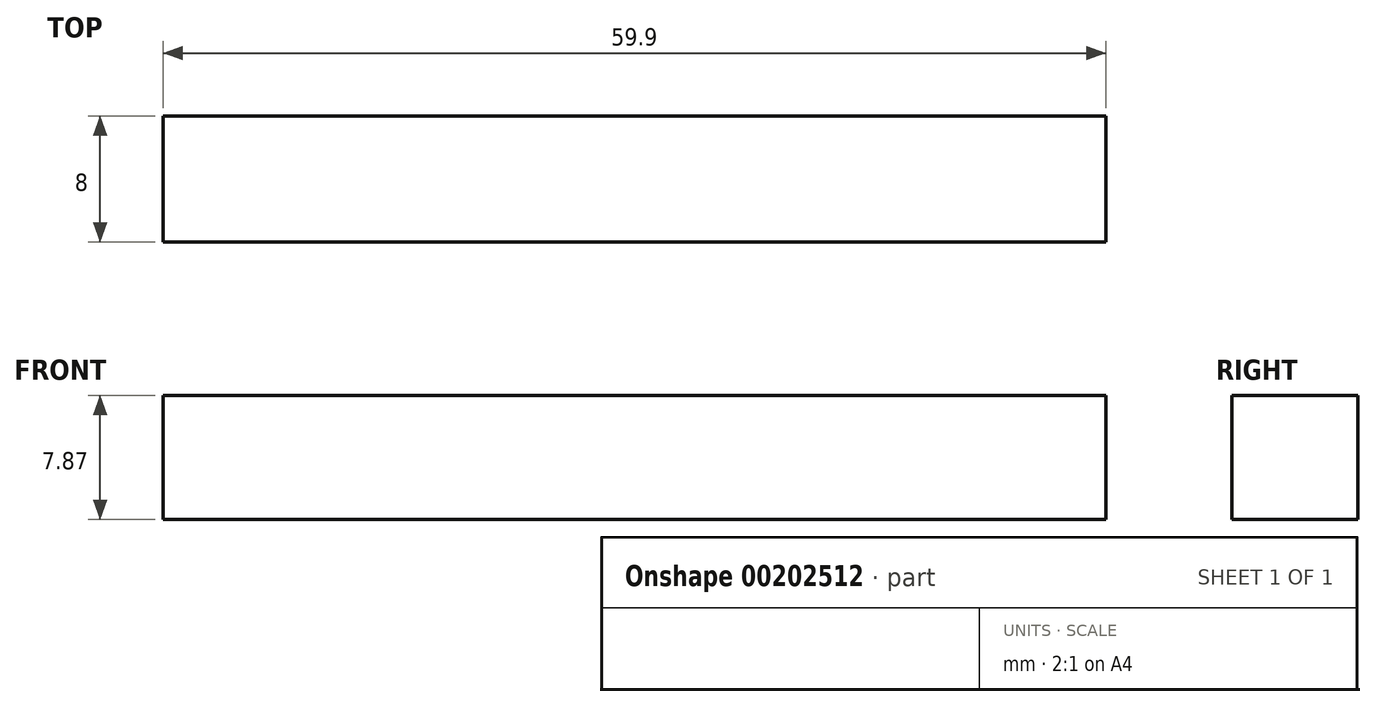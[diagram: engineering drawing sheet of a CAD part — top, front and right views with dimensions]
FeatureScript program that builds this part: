
annotation { "Feature Type Name" : "Feature", "Feature Type Description" : "" }
export const myFeature = defineFeature(function(context is Context, id is Id, definition is map)
    precondition{}
    {
        {
            var Q0;
            Q0=qCreatedBy(makeId("Top.planeOp"),FACE);
            var sketch = newSketch(context, id + "F0", { "sketchPlane" : qUnion([Q0])});
            skLineSegment(sketch, "E0.bottom", {"start": v(45.1, 47.95) * mm, "end": v(-45.1, 47.95) * mm});
            skLineSegment(sketch, "E0.top", {"start": v(45.1, -47.95) * mm, "end": v(-45.1, -47.95) * mm});
            skLineSegment(sketch, "E0.left", {"start": v(45.1, 47.95) * mm, "end": v(45.1, -47.95) * mm});
            skLineSegment(sketch, "E0.right", {"start": v(-45.1, 47.95) * mm, "end": v(-45.1, -47.95) * mm});
            skPoint(sketch, "E0.middle", {"position": v(0, 0) * mm});
            skLineSegment(sketch, "E1.bottom", {"start": v(29.95, 39.05) * mm, "end": v(-29.95, 39.05) * mm});
            skLineSegment(sketch, "E1.top", {"start": v(29.95, 47.05) * mm, "end": v(-29.95, 47.05) * mm});
            skLineSegment(sketch, "E1.left", {"start": v(29.95, 39.05) * mm, "end": v(29.95, 47.05) * mm});
            skLineSegment(sketch, "E1.right", {"start": v(-29.95, 39.05) * mm, "end": v(-29.95, 47.05) * mm});
            skPoint(sketch, "E1.middle", {"position": v(0, 43.05) * mm});
            skSolve(sketch);
        }
        {
            var Q0;
            Q0=makeQuery(id+"F0.imprint","IMPRINT",FACE,{"disambiguationData":[TD([[makeQuery(id+"F0.imprint","IMPRINT",EDGE,{"derivedFrom":sQuery(id+"F0.wireOp",EDGE,"E1.bottom")}),-1.0]])]});
            extrude(context, id + "F1", {"entities" : qUnion([Q0]), "depth" : 7.87 * mm});
        }
    });
